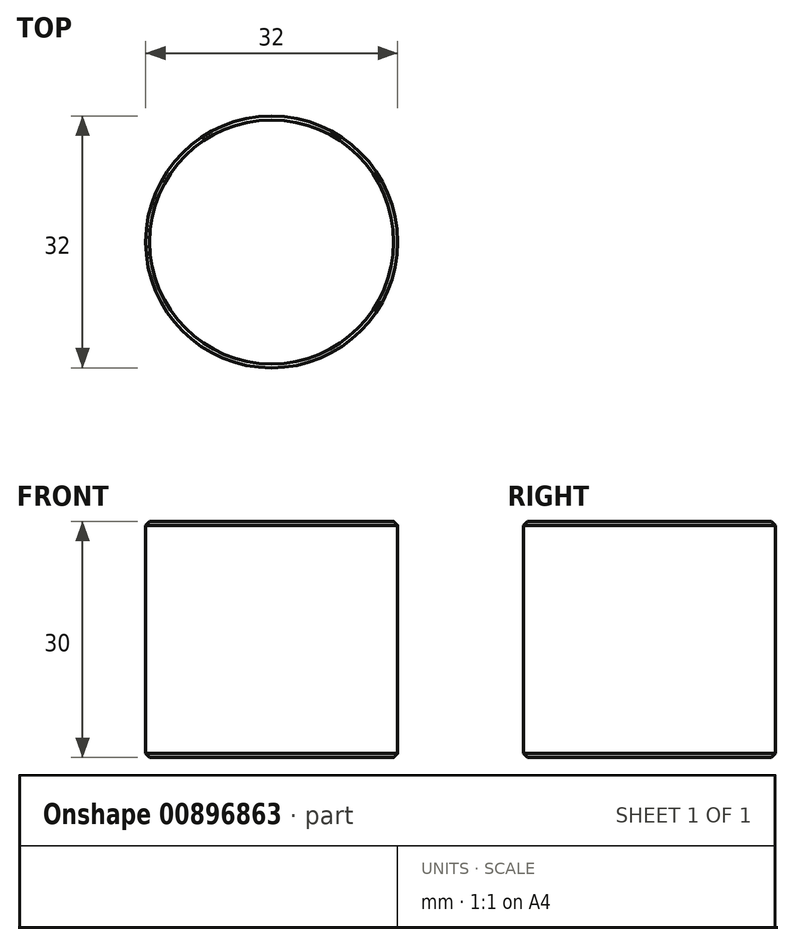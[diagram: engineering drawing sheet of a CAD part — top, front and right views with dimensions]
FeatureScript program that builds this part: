
annotation { "Feature Type Name" : "Feature", "Feature Type Description" : "" }
export const myFeature = defineFeature(function(context is Context, id is Id, definition is map)
    precondition{}
    {
        {
            var Q0;
            Q0=qCreatedBy(makeId("Top.planeOp"),FACE);
            var sketch = newSketch(context, id + "F0", { "sketchPlane" : qUnion([Q0])});
            skCircle(sketch, "E0", {"center": v(0, 0) * mm, "radius": 16 * mm});
            skSolve(sketch);
        }
        {
            var Q0;
            Q0=makeQuery(id+"F0.imprint","IMPRINT",FACE,{"disambiguationData":[TD([[makeQuery(id+"F0.imprint","IMPRINT",EDGE,{"derivedFrom":sQuery(id+"F0.wireOp",EDGE,"E0")}),1.0]])]});
            extrude(context, id + "F1", {"entities" : qUnion([Q0]), "depth" : 30 * mm, "offsetDistance" : 25 * mm});
        }
        {
            var Q0;
            Q0=makeQuery(id+"F1.opExtrude","CAP_FACE",FACE,{"disambiguationData":[OSD([sQuery(id+"F0.wireOp",EDGE,"E0")])],"isStart":false});
            var Q1;
            Q1=makeQuery(id+"F1.opExtrude","CAP_EDGE",EDGE,{"disambiguationData":[OSD([sQuery(id+"F0.wireOp",EDGE,"E0")])],"isStart":true});
            chamfer(context, id + "F2", {"entities" : qUnion([Q0, Q1]), "width" : 0.5 * mm, "tangentPropagation" : true});
        }
    });
